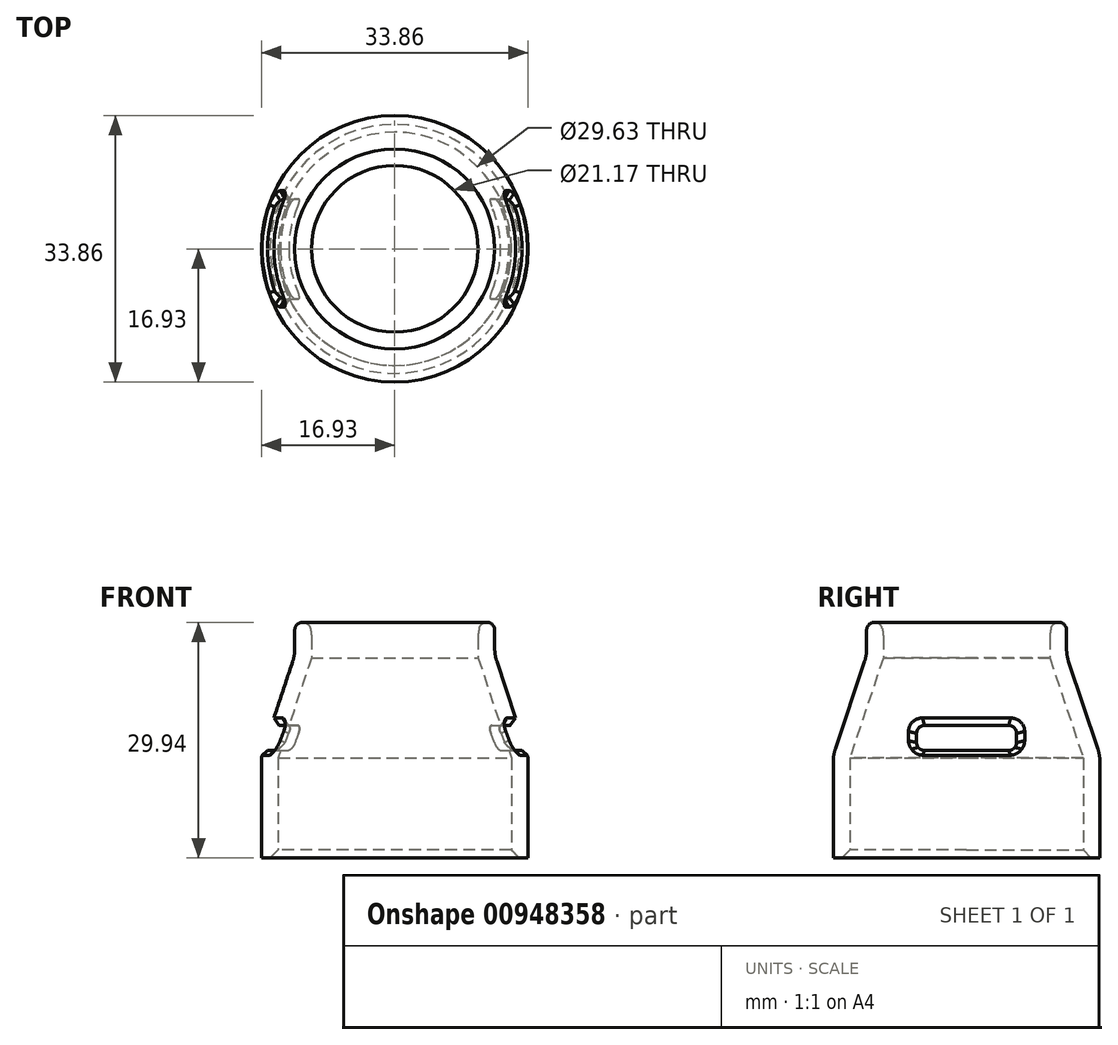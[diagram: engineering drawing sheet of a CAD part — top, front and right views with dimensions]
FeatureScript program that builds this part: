
annotation { "Feature Type Name" : "Feature", "Feature Type Description" : "" }
export const myFeature = defineFeature(function(context is Context, id is Id, definition is map)
    precondition{}
    {
        {
            var Q0;
            Q0=qCreatedBy(makeId("Front.planeOp"),FACE);
            var sketch = newSketch(context, id + "F0", { "sketchPlane" : qUnion([Q0])});
            skPoint(sketch, "E0", {"position": v(-14.82, 0) * mm});
            skPoint(sketch, "E1", {"position": v(-16.93, 0) * mm});
            skLineSegment(sketch, "E2", {"start": v(-14.82, 0) * mm, "end": v(-14.82, 12.7) * mm});
            skLineSegment(sketch, "E3", {"start": v(-14.82, 12.7) * mm, "end": v(-10.58, 25.4) * mm});
            skLineSegment(sketch, "E4", {"start": v(-10.58, 25.4) * mm, "end": v(-10.58, 32.1) * mm});
            skLineSegment(sketch, "E5", {"start": v(-16.93, 0) * mm, "end": v(-16.93, 13.04) * mm});
            skLineSegment(sketch, "E6", {"start": v(-16.93, 13.04) * mm, "end": v(-12.7, 25.74) * mm});
            skLineSegment(sketch, "E7", {"start": v(-12.7, 25.74) * mm, "end": v(-12.7, 32.1) * mm});
            skLineSegment(sketch, "E8", {"start": v(-12.7, 32.1) * mm, "end": v(-10.58, 32.1) * mm});
            skLineSegment(sketch, "E9", {"start": v(-16.93, 0) * mm, "end": v(-14.82, 0) * mm});
            skLineSegment(sketch, "E10", {"start": v(0, 0) * mm, "end": v(0, 80.37) * mm});
            skSolve(sketch);
        }
        {
            var Q0;
            Q0=makeQuery(id+"F0.imprint","IMPRINT",FACE,{"disambiguationData":[TD([[makeQuery(id+"F0.imprint","IMPRINT",EDGE,{"derivedFrom":sQuery(id+"F0.wireOp",EDGE,"E2")}),1.0]])]});
            var Q1;
            Q1=sQuery(id+"F0.wireOp",EDGE,"E10");
            revolve(context, id + "F1", {"surfaceOperationType" : NewSurfaceOperationType.NEW, "entities" : qUnion([Q0]), "axis" : qUnion([Q1]), "revolveType" : RevolveType.FULL});
        }
        {
            var Q0;
            Q0=makeQuery(id+"F1.opRevolve","SWEPT_EDGE",EDGE,{"disambiguationData":[OSD([sQuery(id+"F0.wireOp",EDGE,"E2"),sQuery(id+"F0.wireOp",EDGE,"E9")])]});
            chamfer(context, id + "F2", {"entities" : qUnion([Q0]), "width" : 1 * mm, "tangentPropagation" : true});
        }
        {
            var Q0;
            Q0=makeQuery(id+"F1.opRevolve","SWEPT_EDGE",EDGE,{"disambiguationData":[OSD([sQuery(id+"F0.wireOp",EDGE,"E6"),sQuery(id+"F0.wireOp",EDGE,"E7")])]});
            var Q1;
            Q1=makeQuery(id+"F1.opRevolve","SWEPT_EDGE",EDGE,{"disambiguationData":[OSD([sQuery(id+"F0.wireOp",EDGE,"E5"),sQuery(id+"F0.wireOp",EDGE,"E6")])]});
            var Q2;
            Q2=makeQuery(id+"F1.opRevolve","SWEPT_FACE",FACE,{"disambiguationData":[OSD([sQuery(id+"F0.wireOp",EDGE,"E6")])]});
            fillet(context, id + "F3", {"entities" : qUnion([Q0, Q1, Q2]), "radius" : 5.08 * mm, "tangentPropagation" : true, "allowEdgeOverflow" : false});
        }
        {
            var Q0;
            Q0=qCreatedBy(makeId("Right.planeOp"),FACE);
            var sketch = newSketch(context, id + "F4", { "sketchPlane" : qUnion([Q0])});
            skLineSegment(sketch, "E11.bottom", {"start": v(6.35, 13.65) * mm, "end": v(-6.35, 13.65) * mm});
            skLineSegment(sketch, "E11.top", {"start": v(6.35, 16.83) * mm, "end": v(-6.35, 16.83) * mm});
            skLineSegment(sketch, "E11.left", {"start": v(6.35, 13.65) * mm, "end": v(6.35, 16.83) * mm});
            skLineSegment(sketch, "E11.right", {"start": v(-6.35, 13.65) * mm, "end": v(-6.35, 16.83) * mm});
            skPoint(sketch, "E11.middle", {"position": v(0, 15.24) * mm});
            skSolve(sketch);
        }
        {
            var Q0;
            Q0 = qSketchRegion(id + "F4", true);
            extrude(context, id + "F5", {"entities" : qUnion([Q0]), "operationType" : NewBodyOperationType.REMOVE, "oppositeDirection" : true, "depth" : 55.37 * mm, "offsetDistance" : 25.4 * mm, "symmetric" : true});
        }
        {
            var Q0;
            Q0=makeQuery(id+"F5.boolean.opBoolean","COPY",EDGE,{"disambiguationData":[OD(1.0)],"derivedFrom":makeQuery(id+"F5.opExtrude","SWEPT_EDGE",EDGE,{"disambiguationData":[OSD([sQuery(id+"F4.wireOp",EDGE,"E11.top"),sQuery(id+"F4.wireOp",EDGE,"E11.right")])]})});
            var Q1;
            Q1=makeQuery(id+"F5.boolean.opBoolean","COPY",EDGE,{"disambiguationData":[OD(1.0)],"derivedFrom":makeQuery(id+"F5.opExtrude","SWEPT_EDGE",EDGE,{"disambiguationData":[OSD([sQuery(id+"F4.wireOp",EDGE,"E11.bottom"),sQuery(id+"F4.wireOp",EDGE,"E11.right")])]})});
            var Q2;
            Q2=makeQuery(id+"F5.boolean.opBoolean","COPY",EDGE,{"disambiguationData":[OD(1.0)],"derivedFrom":makeQuery(id+"F5.opExtrude","SWEPT_EDGE",EDGE,{"disambiguationData":[OSD([sQuery(id+"F4.wireOp",EDGE,"E11.bottom"),sQuery(id+"F4.wireOp",EDGE,"E11.left")])]})});
            var Q3;
            Q3=makeQuery(id+"F5.boolean.opBoolean","COPY",EDGE,{"disambiguationData":[OD(1.0)],"derivedFrom":makeQuery(id+"F5.opExtrude","SWEPT_EDGE",EDGE,{"disambiguationData":[OSD([sQuery(id+"F4.wireOp",EDGE,"E11.top"),sQuery(id+"F4.wireOp",EDGE,"E11.left")])]})});
            fillet(context, id + "F6", {"entities" : qUnion([Q0, Q1, Q2, Q3]), "radius" : 1 * mm, "tangentPropagation" : true, "allowEdgeOverflow" : false});
        }
        {
            var Q0;
            Q0=makeQuery(id+"F5.boolean.opBoolean","COPY",EDGE,{"disambiguationData":[OD(0.0)],"derivedFrom":makeQuery(id+"F5.opExtrude","SWEPT_EDGE",EDGE,{"disambiguationData":[OSD([sQuery(id+"F4.wireOp",EDGE,"E11.bottom"),sQuery(id+"F4.wireOp",EDGE,"E11.left")])]})});
            var Q1;
            Q1=makeQuery(id+"F5.boolean.opBoolean","COPY",EDGE,{"disambiguationData":[OD(0.0)],"derivedFrom":makeQuery(id+"F5.opExtrude","SWEPT_EDGE",EDGE,{"disambiguationData":[OSD([sQuery(id+"F4.wireOp",EDGE,"E11.top"),sQuery(id+"F4.wireOp",EDGE,"E11.left")])]})});
            var Q2;
            Q2=makeQuery(id+"F5.boolean.opBoolean","COPY",EDGE,{"disambiguationData":[OD(0.0)],"derivedFrom":makeQuery(id+"F5.opExtrude","SWEPT_EDGE",EDGE,{"disambiguationData":[OSD([sQuery(id+"F4.wireOp",EDGE,"E11.bottom"),sQuery(id+"F4.wireOp",EDGE,"E11.right")])]})});
            var Q3;
            Q3=makeQuery(id+"F5.boolean.opBoolean","COPY",EDGE,{"disambiguationData":[OD(0.0)],"derivedFrom":makeQuery(id+"F5.opExtrude","SWEPT_EDGE",EDGE,{"disambiguationData":[OSD([sQuery(id+"F4.wireOp",EDGE,"E11.top"),sQuery(id+"F4.wireOp",EDGE,"E11.right")])]})});
            fillet(context, id + "F7", {"entities" : qUnion([Q0, Q1, Q2, Q3]), "radius" : 1 * mm, "tangentPropagation" : true, "allowEdgeOverflow" : false});
        }
        {
            var Q0;
            Q0=makeQuery(id+"F5.boolean.opBoolean","INTERSECT",EDGE,{"disambiguationData":[OD(0.0)],"derivedFrom":[makeQuery(id+"F1.opRevolve","SWEPT_FACE",FACE,{"disambiguationData":[OSD([sQuery(id+"F0.wireOp",EDGE,"E6")])]}),makeQuery(id+"F5.opExtrude","SWEPT_FACE",FACE,{"disambiguationData":[OSD([sQuery(id+"F4.wireOp",EDGE,"E11.top")])]})]});
            var Q1;
            Q1=makeQuery(id+"F5.boolean.opBoolean","INTERSECT",EDGE,{"disambiguationData":[OD(0.0)],"derivedFrom":[makeQuery(id+"F3.opFillet","BLEND_FACE",FACE,{"disambiguationData":[OSD([sQuery(id+"F0.wireOp",EDGE,"E5"),sQuery(id+"F0.wireOp",EDGE,"E6")])]}),makeQuery(id+"F5.opExtrude","SWEPT_FACE",FACE,{"disambiguationData":[OSD([sQuery(id+"F4.wireOp",EDGE,"E11.bottom")])]})]});
            var Q2;
            Q2=makeQuery(id+"F5.boolean.opBoolean","INTERSECT",EDGE,{"disambiguationData":[OD(1.0)],"derivedFrom":[makeQuery(id+"F1.opRevolve","SWEPT_FACE",FACE,{"disambiguationData":[OSD([sQuery(id+"F0.wireOp",EDGE,"E6")])]}),makeQuery(id+"F5.opExtrude","SWEPT_FACE",FACE,{"disambiguationData":[OSD([sQuery(id+"F4.wireOp",EDGE,"E11.top")])]})]});
            chamfer(context, id + "F8", {"entities" : qUnion([Q0, Q1, Q2]), "width" : 1 * mm, "tangentPropagation" : true});
        }
        {
            var Q0;
            Q0=makeQuery(id+"F1.opRevolve","SWEPT_EDGE",EDGE,{"disambiguationData":[OSD([sQuery(id+"F0.wireOp",EDGE,"E4"),sQuery(id+"F0.wireOp",EDGE,"E8")])]});
            fillet(context, id + "F9", {"entities" : qUnion([Q0]), "radius" : 5.08 * mm, "tangentPropagation" : true, "allowEdgeOverflow" : false});
        }
        {
            var Q0;
            Q0=makeQuery(id+"F9.opFillet","BLEND_EDGE",EDGE,{"blendedFrom":[makeQuery(id+"F1.opRevolve","SWEPT_EDGE",EDGE,{"disambiguationData":[OSD([sQuery(id+"F0.wireOp",EDGE,"E4"),sQuery(id+"F0.wireOp",EDGE,"E8")])]}),makeQuery(id+"F1.opRevolve","SWEPT_FACE",FACE,{"disambiguationData":[OSD([sQuery(id+"F0.wireOp",EDGE,"E7")])]})],"blendedInto":[makeQuery(id+"F1.opRevolve","SWEPT_FACE",FACE,{"disambiguationData":[OSD([sQuery(id+"F0.wireOp",EDGE,"E7")])]})]});
            fillet(context, id + "F10", {"entities" : qUnion([Q0]), "radius" : 1 * mm, "tangentPropagation" : true, "allowEdgeOverflow" : false});
        }
    });
